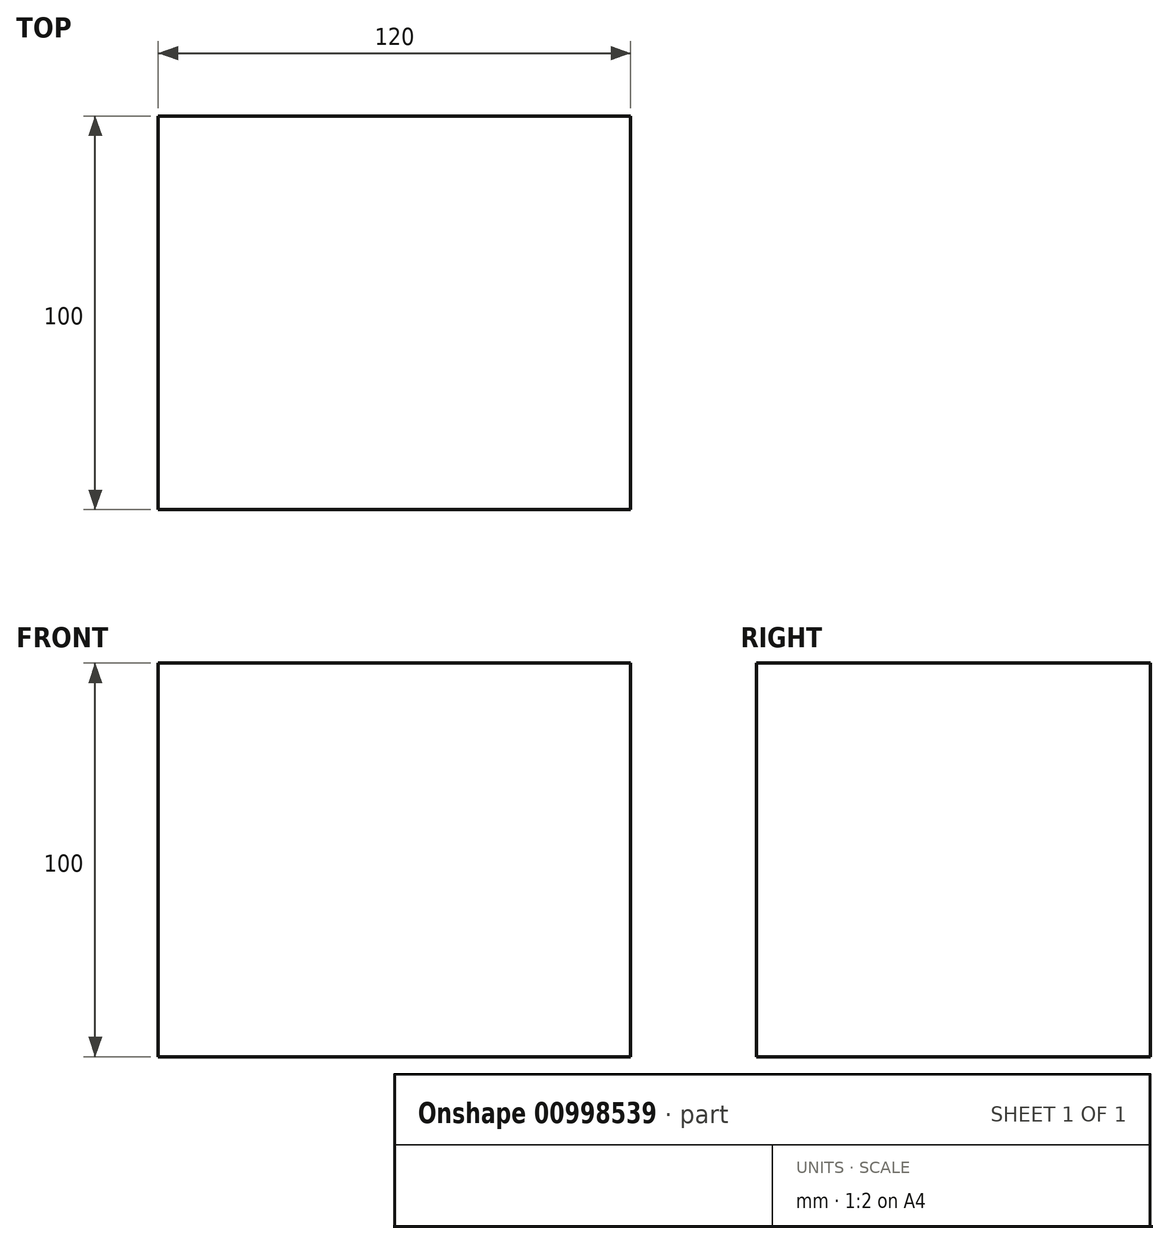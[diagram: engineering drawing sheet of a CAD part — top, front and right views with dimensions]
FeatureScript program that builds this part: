
annotation { "Feature Type Name" : "Feature", "Feature Type Description" : "" }
export const myFeature = defineFeature(function(context is Context, id is Id, definition is map)
    precondition{}
    {
        {
            var Q0;
            Q0=qCreatedBy(makeId("Front.planeOp"),FACE);
            var sketch = newSketch(context, id + "F0", { "sketchPlane" : qUnion([Q0])});
            skLineSegment(sketch, "E0.bottom", {"start": v(0, 0) * mm, "end": v(120, 0) * mm});
            skLineSegment(sketch, "E0.top", {"start": v(0, 100) * mm, "end": v(120, 100) * mm});
            skLineSegment(sketch, "E0.left", {"start": v(0, 0) * mm, "end": v(0, 100) * mm});
            skLineSegment(sketch, "E0.right", {"start": v(120, 0) * mm, "end": v(120, 100) * mm});
            skSolve(sketch);
        }
        {
            var Q0;
            Q0 = qSketchRegion(id + "F0", true);
            extrude(context, id + "F1", {"entities" : qUnion([Q0]), "depth" : 100 * mm, "offsetDistance" : 25 * mm});
        }
    });
